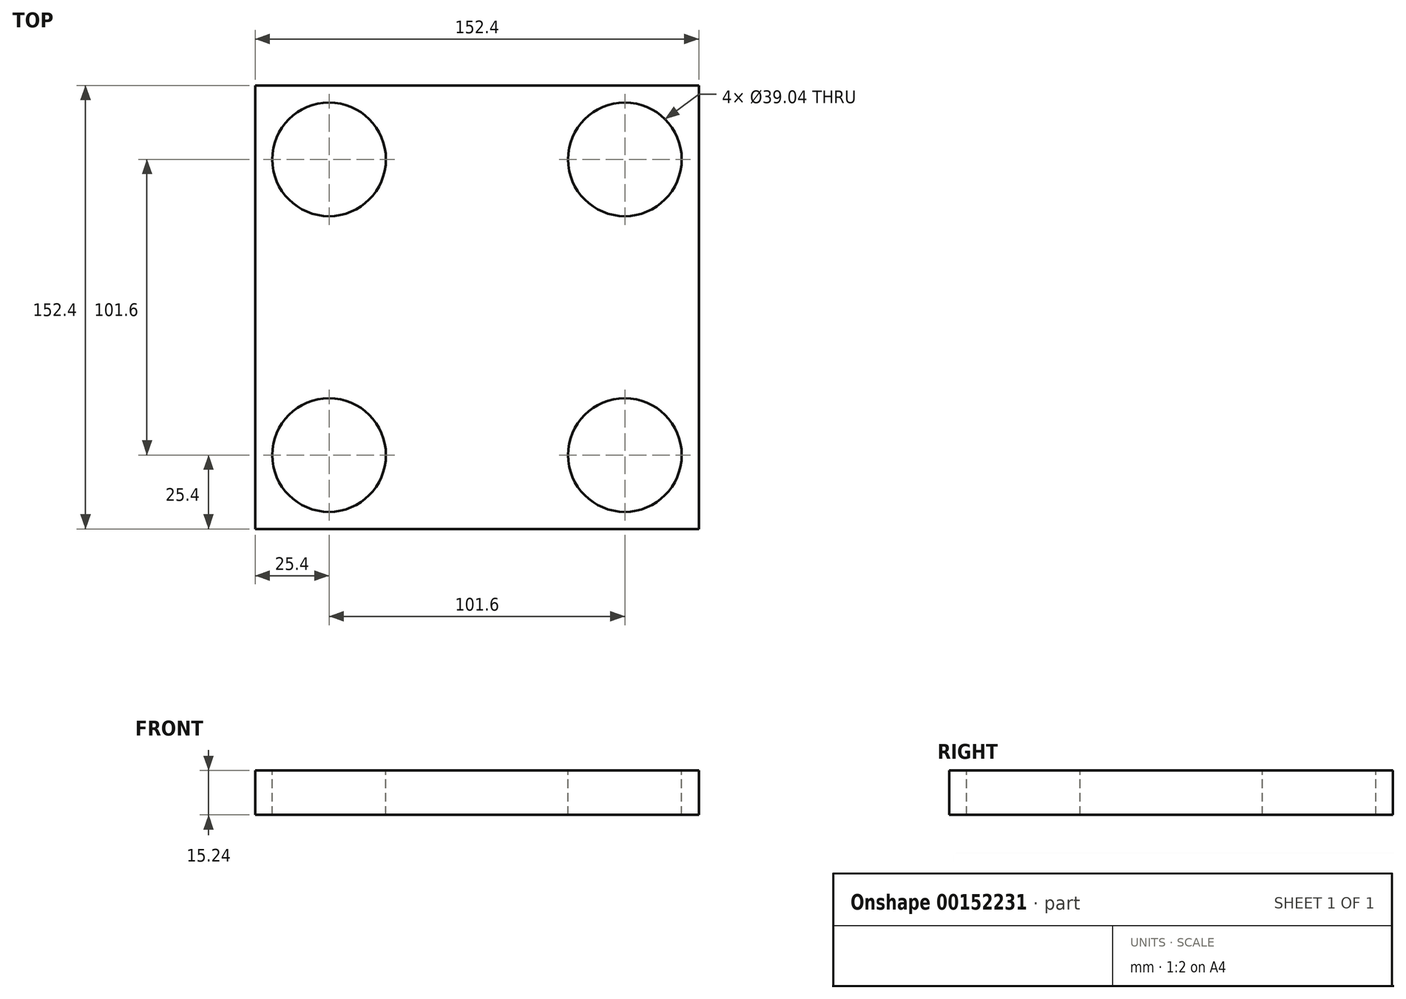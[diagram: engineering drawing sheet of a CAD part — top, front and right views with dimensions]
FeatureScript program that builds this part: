
annotation { "Feature Type Name" : "Feature", "Feature Type Description" : "" }
export const myFeature = defineFeature(function(context is Context, id is Id, definition is map)
    precondition{}
    {
        {
            var Q0;
            Q0=qCreatedBy(makeId("Top.planeOp"),FACE);
            var sketch = newSketch(context, id + "F0", { "sketchPlane" : qUnion([Q0])});
            skCircle(sketch, "E0", {"center": v(-50.8, 50.8) * mm, "radius": 19.52 * mm});
            skCircle(sketch, "E1", {"center": v(50.8, 50.8) * mm, "radius": 19.52 * mm});
            skCircle(sketch, "E2", {"center": v(-50.8, -50.8) * mm, "radius": 19.52 * mm});
            skCircle(sketch, "E3", {"center": v(50.8, -50.8) * mm, "radius": 19.52 * mm});
            skLineSegment(sketch, "E4", {"start": v(-50.8, 50.8) * mm, "end": v(-50.8, -50.8) * mm, "construction": true});
            skLineSegment(sketch, "E5", {"start": v(-50.8, -50.8) * mm, "end": v(50.8, -50.8) * mm, "construction": true});
            skLineSegment(sketch, "E6", {"start": v(50.8, -50.8) * mm, "end": v(50.8, 50.8) * mm, "construction": true});
            skLineSegment(sketch, "E7", {"start": v(50.8, 50.8) * mm, "end": v(-50.8, 50.8) * mm, "construction": true});
            skLineSegment(sketch, "E8", {"start": v(0, 50.8) * mm, "end": v(0, 0) * mm, "construction": true});
            skLineSegment(sketch, "E9", {"start": v(0, -50.8) * mm, "end": v(0, 0) * mm, "construction": true});
            skLineSegment(sketch, "E10", {"start": v(50.8, 0) * mm, "end": v(0, 0) * mm, "construction": true});
            skLineSegment(sketch, "E11.bottom", {"start": v(76.2, 76.2) * mm, "end": v(-76.2, 76.2) * mm});
            skLineSegment(sketch, "E11.top", {"start": v(76.2, -76.2) * mm, "end": v(-76.2, -76.2) * mm});
            skLineSegment(sketch, "E11.left", {"start": v(76.2, 76.2) * mm, "end": v(76.2, -76.2) * mm});
            skLineSegment(sketch, "E11.right", {"start": v(-76.2, 76.2) * mm, "end": v(-76.2, -76.2) * mm});
            skPoint(sketch, "E11.middle", {"position": v(0, 0) * mm});
            skLineSegment(sketch, "E12", {"start": v(-50.8, 0) * mm, "end": v(0, 0) * mm, "construction": true});
            skLineSegment(sketch, "E13", {"start": v(-76.2, 0) * mm, "end": v(0, 0) * mm, "construction": true});
            skLineSegment(sketch, "E14", {"start": v(76.2, 0) * mm, "end": v(0, 0) * mm, "construction": true});
            skLineSegment(sketch, "E15", {"start": v(0, -76.2) * mm, "end": v(0, 0) * mm, "construction": true});
            skLineSegment(sketch, "E16", {"start": v(0, 76.2) * mm, "end": v(0, 0) * mm, "construction": true});
            skSolve(sketch);
        }
        {
            var Q0;
            Q0 = qSketchRegion(id + "F0", true);
            extrude(context, id + "F1", {"entities" : qUnion([Q0]), "oppositeDirection" : true, "depth" : 15.24 * mm});
        }
    });
